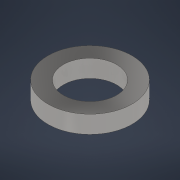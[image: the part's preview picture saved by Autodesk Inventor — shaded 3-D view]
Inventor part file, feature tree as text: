
AUTODESK INVENTOR PART (.ipt)
format: ipt  version: 2021 (Build 250183000, 183)  size: 95,744 bytes
history: native  units: mm
features: extrude x1, sketch x1
ambient origin geometry x8: Origin, YZ Plane, XZ Plane, XY Plane, X Axis, Y Axis, Z Axis, Center Point
bodies: Volumenkörper1 (feature_tree)
feature tree (2):
  extrude  "Extrusion1"  Depth=5.0mm TaperAngle=0.0deg
  sketch  "Skizze1"  dims[d0=24.0mm d2=5.0mm d3=0.0mm d5=15.2mm]
